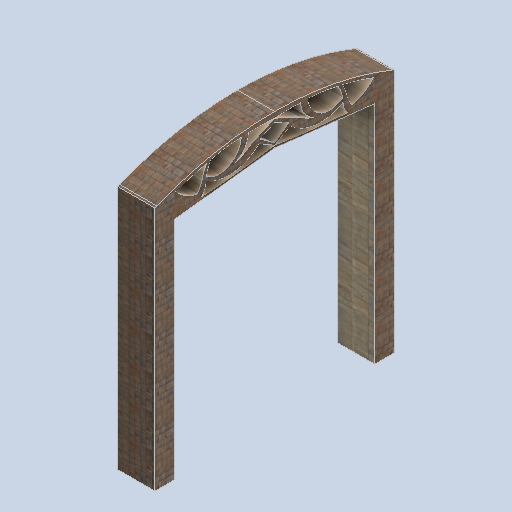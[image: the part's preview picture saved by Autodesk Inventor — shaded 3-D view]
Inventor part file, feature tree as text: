
AUTODESK INVENTOR PART (.ipt)
format: ipt  version: 2024.2 (Build 282272000, 272)  size: 302,592 bytes
history: native  units: in
note: dims shown in document units (in); Inventor stores cm internally (conversion verified against a paired STEP export)
features: other x3, sketch x1
ambient origin geometry x8: Origin, YZ Plane, XZ Plane, XY Plane, X Axis, Y Axis, Z Axis, Center Point
bodies: Solid1 (feature_tree)
feature tree (4):
  other  "side_door_frame.ipt"
  other  "Solid1::side_door_frame.ipt"
  other  "TaggingFeature1"
  sketch  "Sketch1"  dims[d0=0.3937in]
